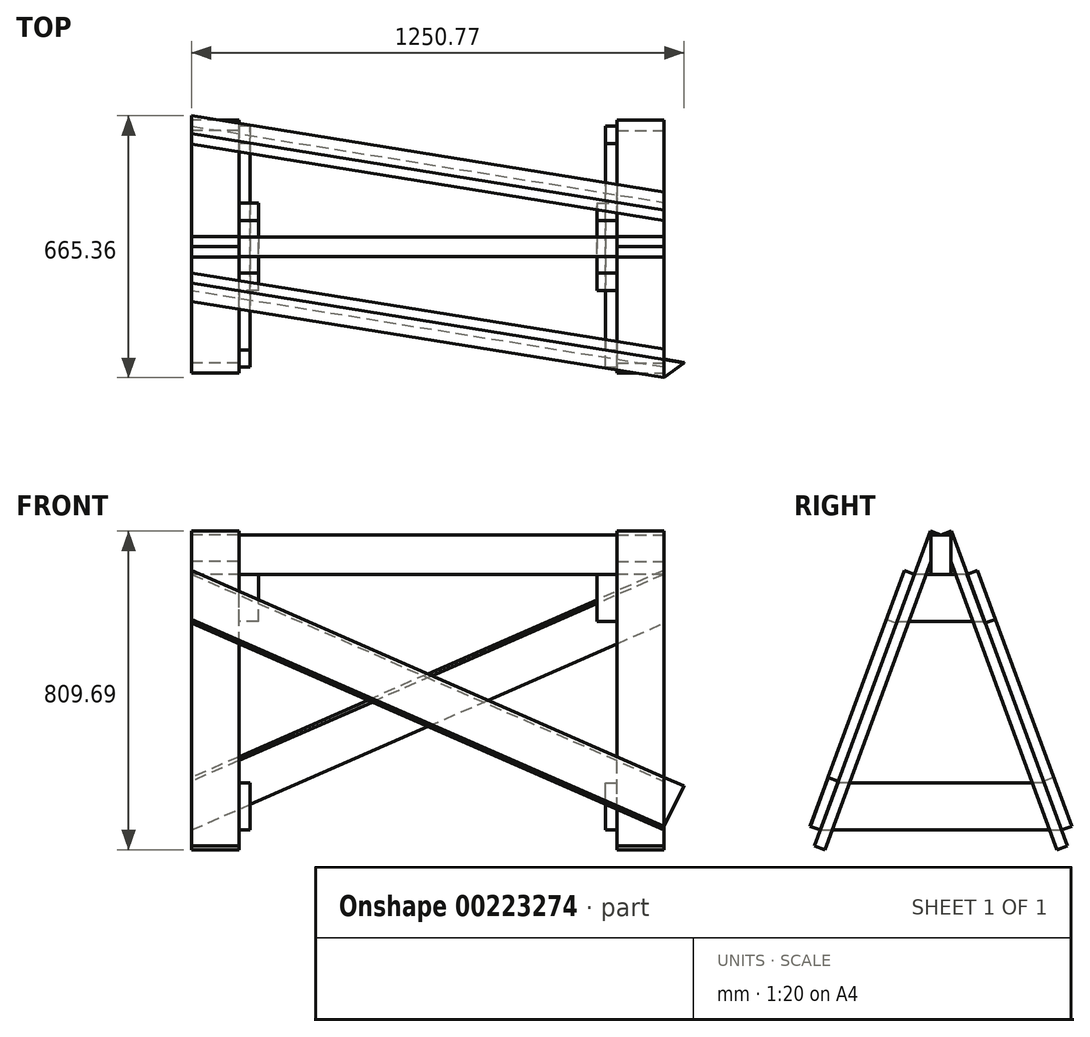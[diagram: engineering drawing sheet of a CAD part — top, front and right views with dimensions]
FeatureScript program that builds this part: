
annotation { "Feature Type Name" : "Feature", "Feature Type Description" : "" }
export const myFeature = defineFeature(function(context is Context, id is Id, definition is map)
    precondition{}
    {
        {
            var Q0;
            Q0=qCreatedBy(makeId("Right.planeOp"),FACE);
            var sketch = newSketch(context, id + "F0", { "sketchPlane" : qUnion([Q0])});
            skLineSegment(sketch, "E0.bottom", {"start": v(-25, 50) * mm, "end": v(25, 50) * mm});
            skLineSegment(sketch, "E0.top", {"start": v(-25, -50) * mm, "end": v(25, -50) * mm});
            skLineSegment(sketch, "E0.left", {"start": v(-25, 50) * mm, "end": v(-25, -50) * mm});
            skLineSegment(sketch, "E0.right", {"start": v(25, 50) * mm, "end": v(25, -50) * mm});
            skPoint(sketch, "E0.middle", {"position": v(0, 0) * mm});
            skLineSegment(sketch, "E1", {"start": v(0, 50) * mm, "end": v(0, -50) * mm, "construction": true});
            skSolve(sketch);
        }
        {
            var Q0;
            Q0=makeQuery(id+"F0.imprint","IMPRINT",FACE,{"disambiguationData":[TD([[makeQuery(id+"F0.imprint","IMPRINT",EDGE,{"derivedFrom":sQuery(id+"F0.wireOp",EDGE,"E0.bottom")}),-1.0]])]});
            extrude(context, id + "F1", {"entities" : qUnion([Q0]), "depth" : 1200 * mm, "symmetric" : true});
        }
        {
            var Q0;
            Q0=makeQuery(id+"F1.opExtrude","CAP_FACE",FACE,{"disambiguationData":[OSD([sQuery(id+"F0.wireOp",EDGE,"E0.bottom"),sQuery(id+"F0.wireOp",EDGE,"E0.top"),sQuery(id+"F0.wireOp",EDGE,"E0.left"),sQuery(id+"F0.wireOp",EDGE,"E0.right")])],"isStart":false});
            var sketch = newSketch(context, id + "F2", { "sketchPlane" : qUnion([Q0])});
            skLineSegment(sketch, "E2", {"start": v(0, 50) * mm, "end": v(-295, -750) * mm});
            skLineSegment(sketch, "E3", {"start": v(-295, -750) * mm, "end": v(-321.27, -740.31) * mm});
            skLineSegment(sketch, "E4", {"start": v(-321.27, -740.31) * mm, "end": v(-26.27, 59.69) * mm});
            skLineSegment(sketch, "E5", {"start": v(-26.27, 59.69) * mm, "end": v(0, 50) * mm});
            skLineSegment(sketch, "E6", {"start": v(0, 50) * mm, "end": v(0, -750) * mm, "construction": true});
            skLineSegment(sketch, "E7", {"start": v(0, 50) * mm, "end": v(295, -750) * mm});
            skLineSegment(sketch, "E8", {"start": v(295, -750) * mm, "end": v(321.27, -740.31) * mm});
            skLineSegment(sketch, "E9", {"start": v(321.27, -740.31) * mm, "end": v(26.27, 59.69) * mm});
            skLineSegment(sketch, "E10", {"start": v(26.27, 59.69) * mm, "end": v(0, 50) * mm});
            skSolve(sketch);
        }
        {
            var Q0;
            {var subQ1=sQuery(id+"F2.wireOp",EDGE,"E3");Q0=makeQuery(id+"F2.imprint","IMPRINT",FACE,{"disambiguationData":[TD([[makeQuery(id+"F2.imprint","IMPRINT",EDGE,{"derivedFrom":subQ1}),-1.0]])]});}
            var Q1;
            {var subQ1=sQuery(id+"F2.wireOp",EDGE,"E8");Q1=makeQuery(id+"F2.imprint","IMPRINT",FACE,{"disambiguationData":[TD([[makeQuery(id+"F2.imprint","IMPRINT",EDGE,{"derivedFrom":subQ1}),1.0]])]});}
            extrude(context, id + "F3", {"entities" : qUnion([Q0, Q1]), "oppositeDirection" : true, "depth" : 120 * mm});
        }
        {
            var Q0;
            Q0=makeQuery(id+"F3.opExtrude","CAP_FACE",FACE,{"disambiguationData":[OSD([sQuery(id+"F0.wireOp",EDGE,"E0.bottom"),sQuery(id+"F0.wireOp",EDGE,"E0.left"),sQuery(id+"F2.wireOp",EDGE,"E2"),sQuery(id+"F2.wireOp",EDGE,"E3"),sQuery(id+"F2.wireOp",EDGE,"E4"),sQuery(id+"F2.wireOp",EDGE,"E5")])],"isStart":false});
            var sketch = newSketch(context, id + "F4", { "sketchPlane" : qUnion([Q0])});
            skLineSegment(sketch, "E11", {"start": v(-66.72, -50) * mm, "end": v(66.72, -50) * mm});
            skLineSegment(sketch, "E12", {"start": v(66.72, -50) * mm, "end": v(110.97, -170) * mm});
            skLineSegment(sketch, "E13", {"start": v(110.97, -170) * mm, "end": v(-110.97, -170) * mm});
            skLineSegment(sketch, "E14", {"start": v(-110.97, -170) * mm, "end": v(-66.72, -50) * mm});
            skSolve(sketch);
        }
        {
            var Q0;
            Q0 = qSketchRegion(id + "F4", true);
            extrude(context, id + "F5", {"entities" : qUnion([Q0]), "depth" : 50 * mm});
        }
        {
            var Q0;
            Q0=makeQuery(id+"F3.opExtrude","CAP_FACE",FACE,{"disambiguationData":[OSD([sQuery(id+"F0.wireOp",EDGE,"E0.bottom"),sQuery(id+"F0.wireOp",EDGE,"E0.left"),sQuery(id+"F2.wireOp",EDGE,"E2"),sQuery(id+"F2.wireOp",EDGE,"E3"),sQuery(id+"F2.wireOp",EDGE,"E4"),sQuery(id+"F2.wireOp",EDGE,"E5")])],"isStart":false});
            var sketch = newSketch(context, id + "F6", { "sketchPlane" : qUnion([Q0])});
            skLineSegment(sketch, "E15", {"start": v(-262.16, -580) * mm, "end": v(262.16, -580) * mm});
            skLineSegment(sketch, "E16", {"start": v(262.16, -580) * mm, "end": v(306.4, -700) * mm});
            skLineSegment(sketch, "E17", {"start": v(306.4, -700) * mm, "end": v(-306.4, -700) * mm});
            skLineSegment(sketch, "E18", {"start": v(-306.4, -700) * mm, "end": v(-262.16, -580) * mm});
            skSolve(sketch);
        }
        {
            var Q0;
            Q0 = qSketchRegion(id + "F6", true);
            extrude(context, id + "F7", {"entities" : qUnion([Q0]), "depth" : 28 * mm});
        }
        {
            var Q0;
            Q0=makeQuery(id+"F3.opExtrude","SWEPT_BODY",BODY,{"disambiguationData":[OSD([sQuery(id+"F0.wireOp",EDGE,"E0.bottom"),sQuery(id+"F0.wireOp",EDGE,"E0.left"),sQuery(id+"F2.wireOp",EDGE,"E2"),sQuery(id+"F2.wireOp",EDGE,"E3"),sQuery(id+"F2.wireOp",EDGE,"E4"),sQuery(id+"F2.wireOp",EDGE,"E5")])]});
            var Q1;
            Q1=makeQuery(id+"F3.opExtrude","SWEPT_BODY",BODY,{"disambiguationData":[OSD([sQuery(id+"F0.wireOp",EDGE,"E0.bottom"),sQuery(id+"F0.wireOp",EDGE,"E0.right"),sQuery(id+"F2.wireOp",EDGE,"E7"),sQuery(id+"F2.wireOp",EDGE,"E8"),sQuery(id+"F2.wireOp",EDGE,"E9"),sQuery(id+"F2.wireOp",EDGE,"E10")])]});
            var Q2;
            Q2=makeQuery(id+"F5.opExtrude","SWEPT_BODY",BODY,{"disambiguationData":[OSD([sQuery(id+"F4.wireOp",EDGE,"E11"),sQuery(id+"F4.wireOp",EDGE,"E12"),sQuery(id+"F4.wireOp",EDGE,"E13"),sQuery(id+"F4.wireOp",EDGE,"E14")])]});
            var Q3;
            Q3=makeQuery(id+"F7.opExtrude","SWEPT_BODY",BODY,{"disambiguationData":[OSD([sQuery(id+"F6.wireOp",EDGE,"E15"),sQuery(id+"F6.wireOp",EDGE,"E16"),sQuery(id+"F6.wireOp",EDGE,"E17"),sQuery(id+"F6.wireOp",EDGE,"E18")])]});
            var Q4;
            Q4=qCreatedBy(makeId("Right.planeOp"),FACE);
            mirror(context, id + "F8", {"entities" : qUnion([Q0, Q1, Q2, Q3]), "mirrorPlane" : qUnion([Q4])});
        }
        {
            var Q0;
            Q0=makeQuery(id+"F3.opExtrude","SWEPT_FACE",FACE,{"disambiguationData":[OSD([sQuery(id+"F2.wireOp",EDGE,"E4")])]});
            var sketch = newSketch(context, id + "F9", { "sketchPlane" : qUnion([Q0])});
            skLineSegment(sketch, "E19", {"start": v(600, -762.78) * mm, "end": v(-600, -202.43) * mm});
            skLineSegment(sketch, "E20", {"start": v(-600, -202.43) * mm, "end": v(-600, -70) * mm});
            skLineSegment(sketch, "E21", {"start": v(-600, -70) * mm, "end": v(600, -630.34) * mm});
            skLineSegment(sketch, "E22", {"start": v(600, -630.34) * mm, "end": v(600, -762.78) * mm});
            skSolve(sketch);
        }
        {
            var Q0;
            Q0 = qSketchRegion(id + "F9", true);
            extrude(context, id + "F10", {"entities" : qUnion([Q0]), "depth" : 28 * mm});
        }
        {
            var Q0;
            Q0=makeQuery(id+"F10.opExtrude","SWEPT_BODY",BODY,{"disambiguationData":[OSD([sQuery(id+"F9.wireOp",EDGE,"E19"),sQuery(id+"F9.wireOp",EDGE,"E20"),sQuery(id+"F9.wireOp",EDGE,"E21"),sQuery(id+"F9.wireOp",EDGE,"E22")])]});
            var Q1;
            Q1=sQuery(id+"F0.wireOp",EDGE,"E1");
            circularPattern(context, id + "F11", {"entities" : qUnion([Q0]), "axis" : qUnion([Q1]), "angle" : 360 * degree, "instanceCount" : 2, "equalSpace" : true});
        }
        {
            var Q0;
            Q0=makeQuery(id+"F10.opExtrude","CAP_FACE",FACE,{"disambiguationData":[OSD([sQuery(id+"F9.wireOp",EDGE,"E19"),sQuery(id+"F9.wireOp",EDGE,"E20"),sQuery(id+"F9.wireOp",EDGE,"E21"),sQuery(id+"F9.wireOp",EDGE,"E22")])],"isStart":false});
            var sketch = newSketch(context, id + "F12", { "sketchPlane" : qUnion([Q0])});
            skLineSegment(sketch, "E23", {"start": v(600, -630.34) * mm, "end": v(650.77, -654.05) * mm});
            skLineSegment(sketch, "E24", {"start": v(650.77, -654.05) * mm, "end": v(600, -762.78) * mm});
            skSolve(sketch);
        }
        {
            var Q0;
            Q0=makeQuery(id+"F12.imprint","IMPRINT",FACE,{"disambiguationData":[TD([[makeQuery(id+"F12.imprint","IMPRINT",EDGE,{"derivedFrom":sQuery(id+"F12.wireOp",EDGE,"E23")}),-1.0]])]});
            extrude(context, id + "F13", {"entities" : qUnion([Q0]), "oppositeDirection" : true, "depth" : 1 * mm});
        }
    });
